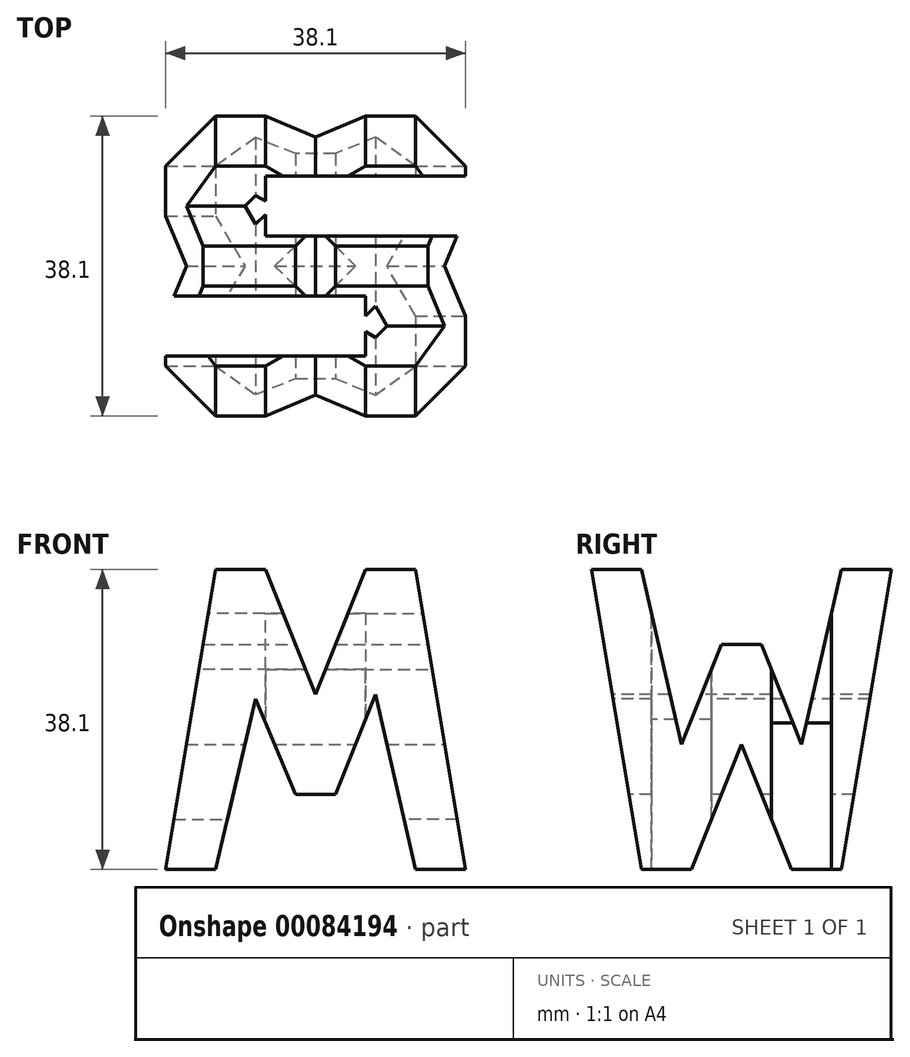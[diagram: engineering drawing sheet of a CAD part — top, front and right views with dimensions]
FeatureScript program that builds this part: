
annotation { "Feature Type Name" : "Feature", "Feature Type Description" : "" }
export const myFeature = defineFeature(function(context is Context, id is Id, definition is map)
    precondition{}
    {
        {
            var Q0;
            Q0=qCreatedBy(makeId("Front.planeOp"),FACE);
            var sketch = newSketch(context, id + "F0", { "sketchPlane" : qUnion([Q0])});
            skLineSegment(sketch, "E0", {"start": v(0, 0) * mm, "end": v(38.1, 0) * mm});
            skLineSegment(sketch, "E1", {"start": v(38.1, 0) * mm, "end": v(38.1, 38.1) * mm});
            skLineSegment(sketch, "E2", {"start": v(38.1, 38.1) * mm, "end": v(0, 38.1) * mm});
            skLineSegment(sketch, "E3", {"start": v(0, 38.1) * mm, "end": v(0, 0) * mm});
            skSolve(sketch);
        }
        {
            var Q0;
            Q0=makeQuery(id+"F0.imprint","IMPRINT",FACE,{"disambiguationData":[TD([[makeQuery(id+"F0.imprint","IMPRINT",EDGE,{"derivedFrom":sQuery(id+"F0.wireOp",EDGE,"E0")}),1.0]])]});
            extrude(context, id + "F1", {"entities" : qUnion([Q0]), "depth" : 38.1 * mm});
        }
        {
            var Q0;
            Q0=qCreatedBy(makeId("Front.planeOp"),FACE);
            cPlane(context, id + "F2", {"entities" : qUnion([Q0]), "cplaneType" : CPlaneType.OFFSET, "offset" : 38.1 * mm, "width" : 152.4 * mm, "height" : 152.4 * mm});
        }
        {
            var Q0;
            Q0=qCreatedBy(makeId("Right.planeOp"),FACE);
            cPlane(context, id + "F3", {"entities" : qUnion([Q0]), "cplaneType" : CPlaneType.OFFSET, "offset" : 38.1 * mm, "width" : 152.4 * mm, "height" : 152.4 * mm});
        }
        {
            var Q0;
            Q0=qCreatedBy(makeId("Top.planeOp"),FACE);
            cPlane(context, id + "F4", {"entities" : qUnion([Q0]), "cplaneType" : CPlaneType.OFFSET, "offset" : 38.1 * mm, "width" : 152.4 * mm, "height" : 152.4 * mm});
        }
        {
            var Q0;
            Q0=qCreatedBy(id+"F3.planeOp",FACE);
            var sketch = newSketch(context, id + "F5", { "sketchPlane" : qUnion([Q0])});
            skLineSegment(sketch, "E4", {"start": v(-38.1, 38.1) * mm, "end": v(-31.75, 38.1) * mm});
            skLineSegment(sketch, "E5", {"start": v(-6.35, 38.1) * mm, "end": v(0, 38.1) * mm});
            skLineSegment(sketch, "E6", {"start": v(0, 38.1) * mm, "end": v(-6.35, 0) * mm});
            skLineSegment(sketch, "E7", {"start": v(-6.35, 0) * mm, "end": v(-12.7, 0) * mm});
            skLineSegment(sketch, "E8", {"start": v(-12.7, 0) * mm, "end": v(-19.05, 15.88) * mm});
            skLineSegment(sketch, "E9", {"start": v(-19.05, 15.88) * mm, "end": v(-25.4, 0) * mm});
            skLineSegment(sketch, "E10", {"start": v(-25.4, 0) * mm, "end": v(-31.75, 0) * mm});
            skLineSegment(sketch, "E11", {"start": v(-31.75, 0) * mm, "end": v(-38.1, 38.1) * mm});
            skLineSegment(sketch, "E12", {"start": v(-21.59, 28.57) * mm, "end": v(-16.5, 28.57) * mm});
            skLineSegment(sketch, "E13", {"start": v(-16.5, 28.58) * mm, "end": v(-11.43, 15.88) * mm});
            skLineSegment(sketch, "E14", {"start": v(-11.43, 15.87) * mm, "end": v(-6.35, 38.1) * mm});
            skLineSegment(sketch, "E15", {"start": v(-31.75, 38.1) * mm, "end": v(-26.67, 15.88) * mm});
            skLineSegment(sketch, "E16", {"start": v(-26.67, 15.88) * mm, "end": v(-21.59, 28.57) * mm});
            skLineSegment(sketch, "E17.bottom", {"start": v(0, 0) * mm, "end": v(-38.1, 0) * mm});
            skLineSegment(sketch, "E17.top", {"start": v(0, 38.1) * mm, "end": v(-38.1, 38.1) * mm});
            skLineSegment(sketch, "E17.left", {"start": v(0, 0) * mm, "end": v(0, 38.1) * mm});
            skLineSegment(sketch, "E17.right", {"start": v(-38.1, 0) * mm, "end": v(-38.1, 38.1) * mm});
            skSolve(sketch);
        }
        {
            var Q0;
            Q0=makeQuery(id+"F5.imprint","IMPRINT",FACE,{"disambiguationData":[TD([[makeQuery(id+"F5.imprint","IMPRINT",EDGE,{"derivedFrom":sQuery(id+"F5.wireOp",EDGE,"E12")}),1.0]])]});
            var Q1;
            {var subQ0=sQuery(id+"F5.wireOp",EDGE,"E8");Q1=makeQuery(id+"F5.imprint","IMPRINT",FACE,{"disambiguationData":[TD([[makeQuery(id+"F5.imprint","IMPRINT",EDGE,{"derivedFrom":subQ0}),1.0]])]});}
            var Q2;
            {var subQ0=sQuery(id+"F5.wireOp",EDGE,"E11");Q2=makeQuery(id+"F5.imprint","IMPRINT",FACE,{"disambiguationData":[TD([[makeQuery(id+"F5.imprint","IMPRINT",EDGE,{"derivedFrom":subQ0}),1.0]])]});}
            var Q3;
            {var subQ0=sQuery(id+"F5.wireOp",EDGE,"E6");Q3=makeQuery(id+"F5.imprint","IMPRINT",FACE,{"disambiguationData":[TD([[makeQuery(id+"F5.imprint","IMPRINT",EDGE,{"derivedFrom":subQ0}),1.0]])]});}
            extrude(context, id + "F6", {"entities" : qUnion([Q0, Q1, Q2, Q3]), "operationType" : NewBodyOperationType.REMOVE, "oppositeDirection" : true, "depth" : 38.1 * mm});
        }
        {
            var Q0;
            Q0=qCreatedBy(id+"F2.planeOp",FACE);
            var sketch = newSketch(context, id + "F7", { "sketchPlane" : qUnion([Q0])});
            skLineSegment(sketch, "E18.bottom", {"start": v(0, 0) * mm, "end": v(38.1, 0) * mm});
            skLineSegment(sketch, "E18.top", {"start": v(0, 38.1) * mm, "end": v(38.1, 38.1) * mm});
            skLineSegment(sketch, "E18.left", {"start": v(0, 0) * mm, "end": v(0, 38.1) * mm});
            skLineSegment(sketch, "E18.right", {"start": v(38.1, 0) * mm, "end": v(38.1, 38.1) * mm});
            skLineSegment(sketch, "E19", {"start": v(0, 0) * mm, "end": v(6.35, 38.1) * mm});
            skLineSegment(sketch, "E20", {"start": v(6.35, 38.1) * mm, "end": v(12.7, 38.1) * mm});
            skLineSegment(sketch, "E21", {"start": v(12.7, 38.1) * mm, "end": v(19.05, 22.23) * mm});
            skLineSegment(sketch, "E22", {"start": v(19.05, 22.23) * mm, "end": v(25.4, 38.1) * mm});
            skLineSegment(sketch, "E23", {"start": v(25.4, 38.1) * mm, "end": v(31.75, 38.1) * mm});
            skLineSegment(sketch, "E24", {"start": v(31.75, 38.1) * mm, "end": v(38.1, 0) * mm});
            skLineSegment(sketch, "E25", {"start": v(31.75, 0) * mm, "end": v(26.67, 22.22) * mm});
            skLineSegment(sketch, "E26", {"start": v(26.67, 22.22) * mm, "end": v(21.6, 9.52) * mm});
            skLineSegment(sketch, "E27", {"start": v(21.6, 9.53) * mm, "end": v(16.51, 9.52) * mm});
            skLineSegment(sketch, "E28", {"start": v(16.51, 9.52) * mm, "end": v(11.43, 21.64) * mm});
            skLineSegment(sketch, "E29", {"start": v(11.43, 21.64) * mm, "end": v(6.35, 0) * mm});
            skLineSegment(sketch, "E30", {"start": v(0, 0) * mm, "end": v(6.35, 0) * mm});
            skSolve(sketch);
        }
        {
            var Q0;
            {var subQ0=sQuery(id+"F7.wireOp",EDGE,"E18.left");Q0=makeQuery(id+"F7.imprint","IMPRINT",FACE,{"disambiguationData":[TD([[makeQuery(id+"F7.imprint","IMPRINT",EDGE,{"derivedFrom":subQ0}),-1.0]])]});}
            var Q1;
            {var subQ0=sQuery(id+"F7.wireOp",EDGE,"E21");Q1=makeQuery(id+"F7.imprint","IMPRINT",FACE,{"disambiguationData":[TD([[makeQuery(id+"F7.imprint","IMPRINT",EDGE,{"derivedFrom":subQ0}),1.0]])]});}
            var Q2;
            {var subQ0=sQuery(id+"F7.wireOp",EDGE,"E18.right");Q2=makeQuery(id+"F7.imprint","IMPRINT",FACE,{"disambiguationData":[TD([[makeQuery(id+"F7.imprint","IMPRINT",EDGE,{"derivedFrom":subQ0}),1.0]])]});}
            var Q3;
            {var subQ2=sQuery(id+"F7.wireOp",EDGE,"E25");Q3=makeQuery(id+"F7.imprint","IMPRINT",FACE,{"disambiguationData":[TD([[makeQuery(id+"F7.imprint","IMPRINT",EDGE,{"derivedFrom":subQ2}),1.0]])]});}
            extrude(context, id + "F8", {"entities" : qUnion([Q0, Q1, Q2, Q3]), "operationType" : NewBodyOperationType.REMOVE, "oppositeDirection" : true, "depth" : 38.1 * mm});
        }
        {
            var Q0;
            Q0=qCreatedBy(id+"F4.planeOp",FACE);
            var sketch = newSketch(context, id + "F9", { "sketchPlane" : qUnion([Q0])});
            skLineSegment(sketch, "E31.bottom", {"start": v(0, 0) * mm, "end": v(38.1, 0) * mm});
            skLineSegment(sketch, "E31.top", {"start": v(0, -38.1) * mm, "end": v(38.1, -38.1) * mm});
            skLineSegment(sketch, "E31.left", {"start": v(0, 0) * mm, "end": v(0, -38.1) * mm});
            skLineSegment(sketch, "E31.right", {"start": v(38.1, 0) * mm, "end": v(38.1, -38.1) * mm});
            skLineSegment(sketch, "E32.bottom", {"start": v(38.1, -7.62) * mm, "end": v(12.7, -7.62) * mm});
            skLineSegment(sketch, "E32.top", {"start": v(38.1, -15.24) * mm, "end": v(12.7, -15.24) * mm});
            skLineSegment(sketch, "E32.left", {"start": v(38.1, -7.62) * mm, "end": v(38.1, -15.24) * mm});
            skLineSegment(sketch, "E32.right", {"start": v(12.7, -7.62) * mm, "end": v(12.7, -15.24) * mm});
            skLineSegment(sketch, "E33.bottom", {"start": v(0, -22.86) * mm, "end": v(25.4, -22.86) * mm});
            skLineSegment(sketch, "E33.top", {"start": v(0, -30.48) * mm, "end": v(25.4, -30.48) * mm});
            skLineSegment(sketch, "E33.left", {"start": v(0, -22.86) * mm, "end": v(0, -30.48) * mm});
            skLineSegment(sketch, "E33.right", {"start": v(25.4, -22.86) * mm, "end": v(25.4, -30.48) * mm});
            skSolve(sketch);
        }
        {
            var Q0;
            Q0=makeQuery(id+"F9.imprint","IMPRINT",FACE,{"disambiguationData":[TD([[makeQuery(id+"F9.imprint","IMPRINT",EDGE,{"derivedFrom":sQuery(id+"F9.wireOp",EDGE,"E32.bottom")}),1.0]])]});
            var Q1;
            Q1=makeQuery(id+"F9.imprint","IMPRINT",FACE,{"disambiguationData":[TD([[makeQuery(id+"F9.imprint","IMPRINT",EDGE,{"derivedFrom":sQuery(id+"F9.wireOp",EDGE,"E33.bottom")}),-1.0]])]});
            extrude(context, id + "F10", {"entities" : qUnion([Q0, Q1]), "operationType" : NewBodyOperationType.REMOVE, "oppositeDirection" : true, "depth" : 38.1 * mm});
        }
    });
